# Revit family: IVLB_Trilux_LF_LnPlus 40_aluminium
name_source: partatom
category: Lighting Fixtures
units: mm (PartAtom-declared; Revit-internal decimal feet)

## family parameters
Always vertical = No
Cut with Voids When Loaded = No
Light Source = No
Part Type = Normal
Room Calculation Point = No
Round Connector Dimension = Use Diameter
Shared = No
Work Plane-Based = No

## types (8) — shared parameters
Assembly Code = 63.0
Bracket_Material = TRILUX_RAL9006
Housing_Material = TRILUX_DB703
IK Value = IK09
IP Value = IP66
IfcExportAs = IfcLightFixtureType
IfcExportType = USERDEFINED
Lamp = LED
Manufacturer = TRILUX GmbH & Co. KG
Model = LnPlus 40
Type Image = Lumena_Plus_S_an_39320_DB_WEB.jpg
URL = https://www.trilux.com
Voltage = 230 V

## per-type parameters (varying)
| type | Apparent Load | EAN Code | LightSource | Luminous Flux (lm) | TOC | Type Comments | Wattage Comments |
| TX376932 | 22 VA | 4018242669196 | LnPlus_40_LS : TX376932 | 3200 lm | 8135751 | AB7L/3200-740 4G1 ETDD | 22W |
| TX377702 | 23 VA | 4018242669196 | LnPlus_40_LS : TX377302 | 3200 lm | 8135751 | AB7L/3200-740 4G1 ETDD | 23W |
| TX377220 | 56 VA | 4018242669318 | LnPlus_40_LS : TX377220 | 8200 lm | 8136951 | AB7L/3200-740 4G1 ETDD | 56W |
| TX377547 | 59 VA | 4018242669318 | LnPlus_40_LS : TX377547 | 8200 lm | 8136951 | AB7L8200-740 8G1 ETDD | 59W |
| TX376945 | 22 VA | 4018242667703 | LnPlus_40_LS : TX376945 | 3200 lm | 8120851 | AM19L3200-740 4G1 ETDD | 22W |
| TX377401 | 23 VA | 4018242667703 | LnPlus_40_LS : TX377401 | 3200 lm | 8120851 | AM19L3200-740 4G1 ETDD | 23W |
| TX376869 | 59 VA | 4018242667734 | LnPlus_40_LS : TX376869 | 8200 lm | 8121151 | AM19L8200-740 8G1 ETDD | 59W |
| TX377302 | 56 VA | 4018242667734 | LnPlus_40_LS : TX377302 | 8200 lm | 8121151 | AM19L8200-740 8G1 ETDD | 56W |

## geometry (parser evidence)
native form markers: Sweep x11
no freeform markers — native parametric forms only
